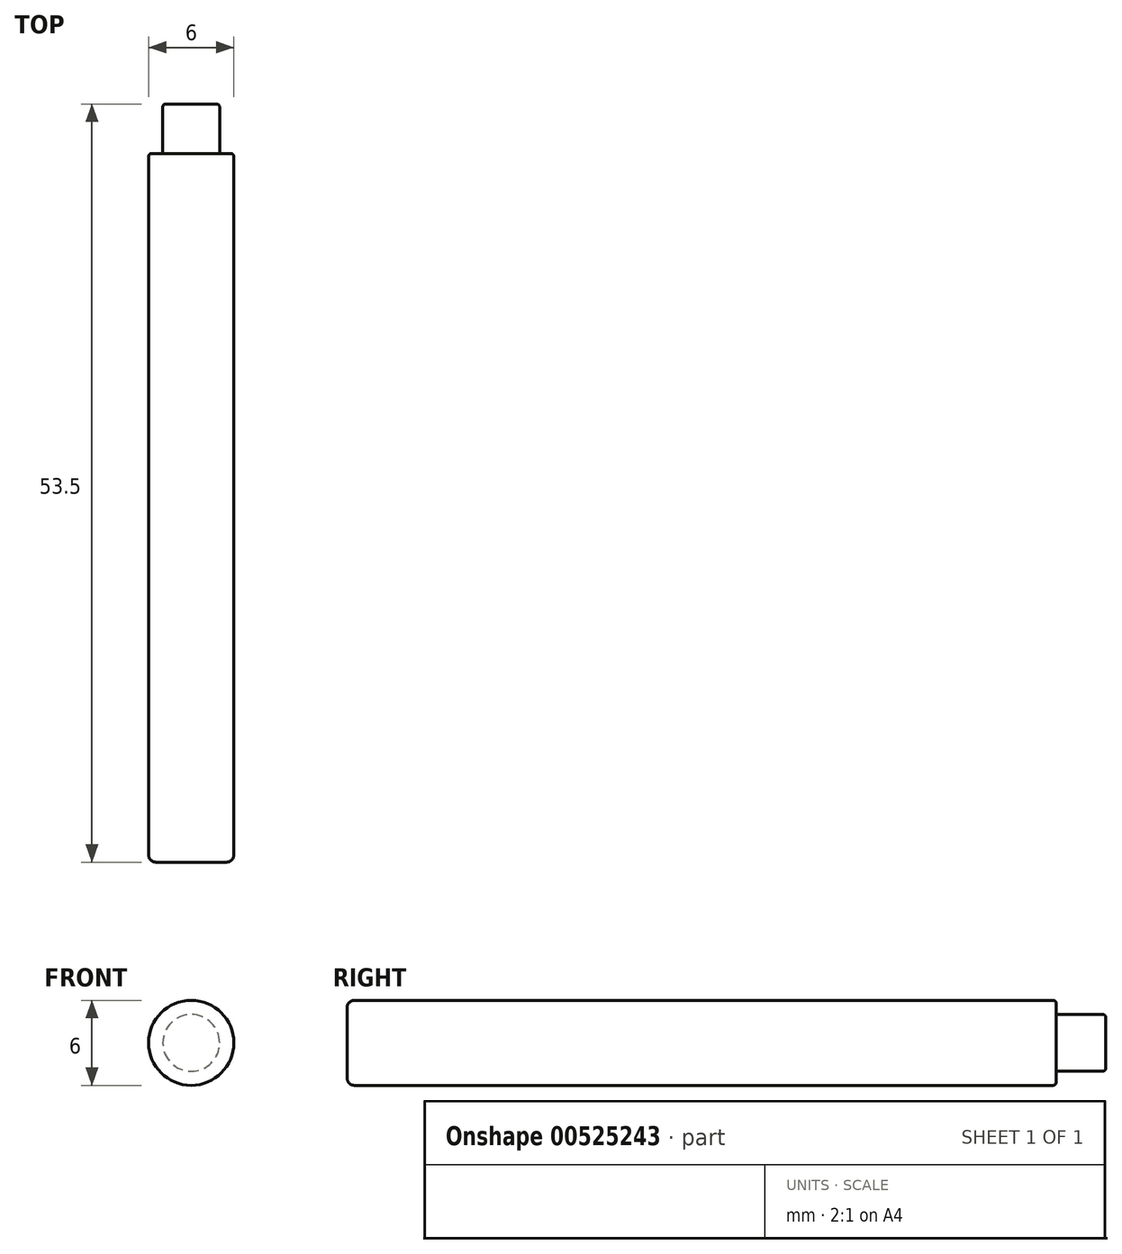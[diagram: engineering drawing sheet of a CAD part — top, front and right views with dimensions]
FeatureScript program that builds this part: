
annotation { "Feature Type Name" : "Feature", "Feature Type Description" : "" }
export const myFeature = defineFeature(function(context is Context, id is Id, definition is map)
    precondition{}
    {
        {
            var Q0;
            Q0=qCreatedBy(makeId("Front.planeOp"),FACE);
            var sketch = newSketch(context, id + "F0", { "sketchPlane" : qUnion([Q0])});
            skCircle(sketch, "E0", {"center": v(0, 0) * mm, "radius": 3 * mm});
            skSolve(sketch);
        }
        {
            var Q0;
            Q0=makeQuery(id+"F0.imprint","IMPRINT",FACE,{"disambiguationData":[TD([[makeQuery(id+"F0.imprint","IMPRINT",EDGE,{"derivedFrom":sQuery(id+"F0.wireOp",EDGE,"E0")}),1.0]])]});
            extrude(context, id + "F1", {"entities" : qUnion([Q0]), "depth" : 50 * mm, "offsetDistance" : 25 * mm});
        }
        {
            var Q0;
            Q0=qCreatedBy(makeId("Front.planeOp"),FACE);
            var sketch = newSketch(context, id + "F2", { "sketchPlane" : qUnion([Q0])});
            skCircle(sketch, "E1", {"center": v(0, 0) * mm, "radius": 2 * mm});
            skLineSegment(sketch, "E2", {"start": v(0, 2) * mm, "end": v(0, -2) * mm, "construction": true});
            skLineSegment(sketch, "E3", {"start": v(2, 0) * mm, "end": v(-2, 0) * mm, "construction": true});
            skSolve(sketch);
        }
        {
            var Q0;
            Q0=makeQuery(id+"F2.imprint","IMPRINT",FACE,{"disambiguationData":[TD([[makeQuery(id+"F2.imprint","IMPRINT",EDGE,{"derivedFrom":sQuery(id+"F2.wireOp",EDGE,"E1")}),1.0]])]});
            extrude(context, id + "F3", {"entities" : qUnion([Q0]), "flatOperationType" : FlatOperationType.REMOVE, "oppositeDirection" : true, "depth" : 3.5 * mm, "offsetDistance" : 25 * mm, "domain" : OperationDomain.MODEL});
        }
        {
            var Q0;
            Q0=makeQuery(id+"F1.opExtrude","CAP_EDGE",EDGE,{"disambiguationData":[OSD([sQuery(id+"F0.wireOp",EDGE,"E0")])],"isStart":true});
            var Q1;
            Q1=makeQuery(id+"F3.opExtrude","CAP_EDGE",EDGE,{"disambiguationData":[OSD([sQuery(id+"F2.wireOp",EDGE,"E1")])],"isStart":false});
            fillet(context, id + "F4", {"entities" : qUnion([Q0, Q1]), "radius" : 0.2 * mm, "tangentPropagation" : true, "allowEdgeOverflow" : false});
        }
        {
            var Q0;
            Q0=makeQuery(id+"F1.opExtrude","CAP_EDGE",EDGE,{"disambiguationData":[OSD([sQuery(id+"F0.wireOp",EDGE,"E0")])],"isStart":false});
            fillet(context, id + "F5", {"entities" : qUnion([Q0]), "radius" : 0.5 * mm, "tangentPropagation" : true, "allowEdgeOverflow" : false});
        }
    });
